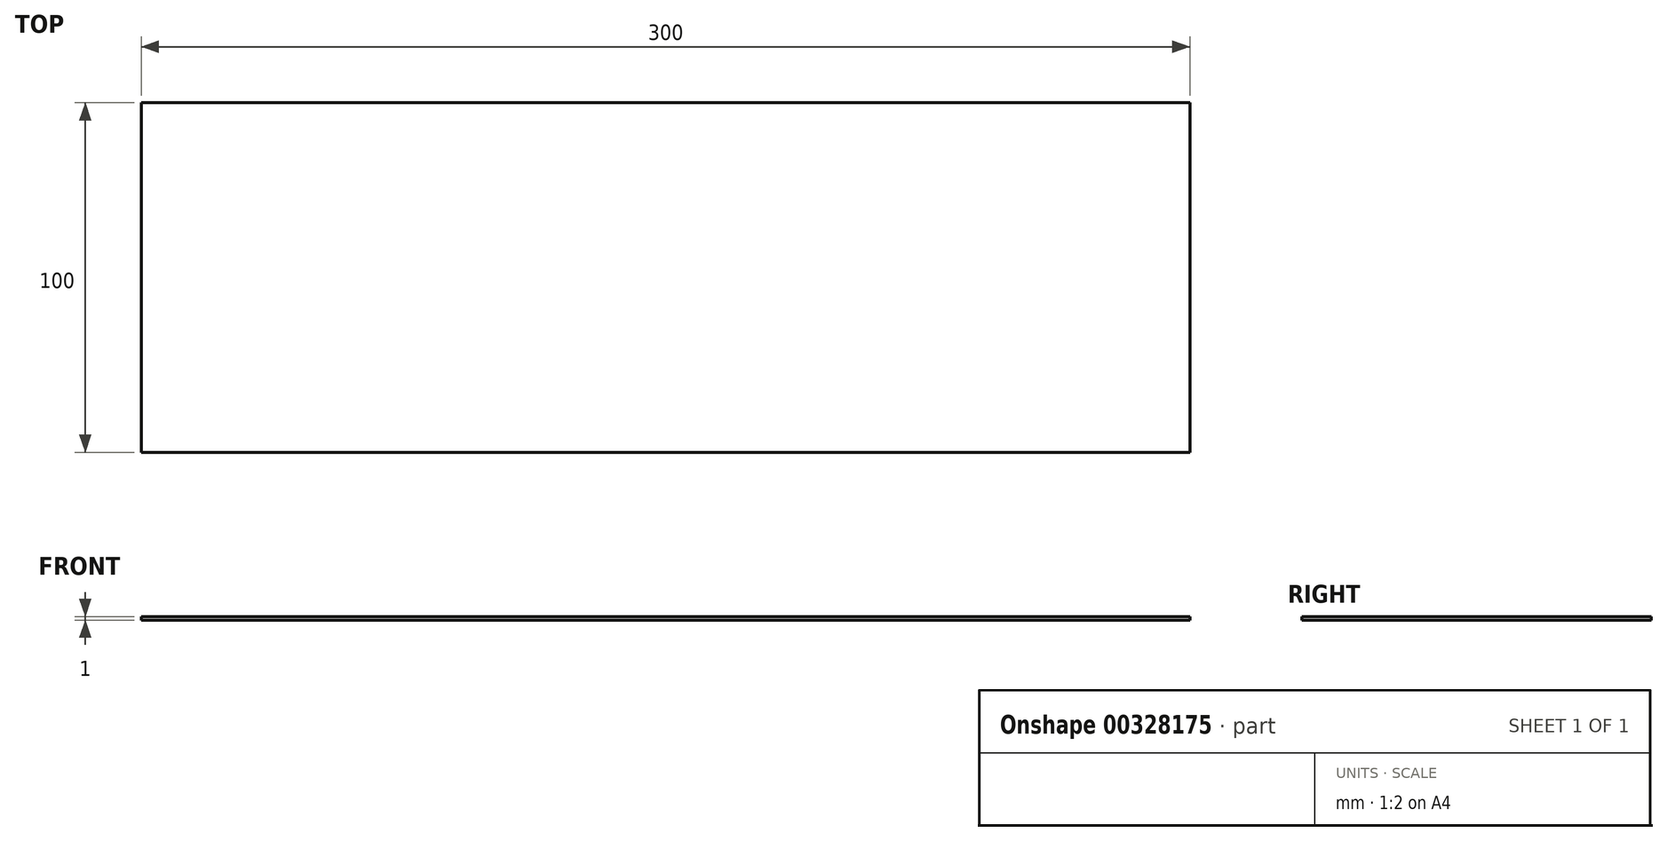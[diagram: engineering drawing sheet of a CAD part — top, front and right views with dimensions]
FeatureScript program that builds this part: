
annotation { "Feature Type Name" : "Feature", "Feature Type Description" : "" }
export const myFeature = defineFeature(function(context is Context, id is Id, definition is map)
    precondition{}
    {
        {
            var Q0;
            Q0=qCreatedBy(makeId("Top.planeOp"),FACE);
            var sketch = newSketch(context, id + "F0", { "sketchPlane" : qUnion([Q0])});
            skLineSegment(sketch, "E0", {"start": v(-49.72, 51.6) * mm, "end": v(-49.72, -48.4) * mm});
            skLineSegment(sketch, "E1", {"start": v(-49.72, -48.4) * mm, "end": v(250.28, -48.4) * mm});
            skLineSegment(sketch, "E2", {"start": v(250.28, -48.4) * mm, "end": v(250.28, 51.6) * mm});
            skLineSegment(sketch, "E3", {"start": v(250.28, 51.6) * mm, "end": v(-49.72, 51.6) * mm});
            skSolve(sketch);
        }
        {
            var Q0;
            Q0=makeQuery(id+"F0.imprint","IMPRINT",FACE,{"disambiguationData":[TD([[makeQuery(id+"F0.imprint","IMPRINT",EDGE,{"derivedFrom":sQuery(id+"F0.wireOp",EDGE,"E0")}),1.0]])]});
            extrude(context, id + "F1", {"entities" : qUnion([Q0]), "depth" : 1 * mm});
        }
    });
